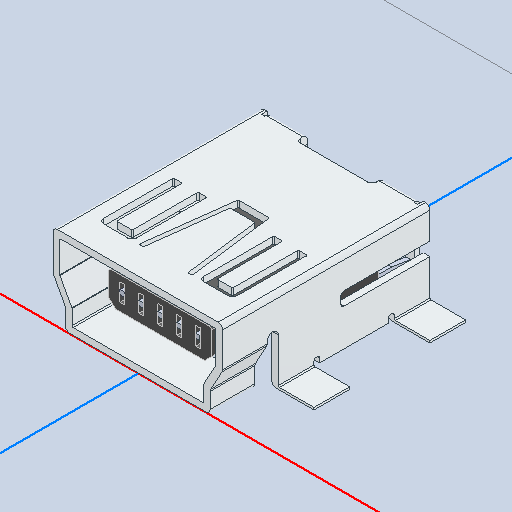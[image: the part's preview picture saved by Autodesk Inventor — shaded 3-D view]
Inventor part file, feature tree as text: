
AUTODESK INVENTOR PART (.ipt)
format: ipt  version: 2022 (Build 260153000, 153)  size: 313,856 bytes
history: native  units: mm
features: other x12, fillet x1, chamfer x1
ambient origin geometry x8: Origin, YZ Plane, XZ Plane, XY Plane, X Axis, Y Axis, Z Axis, Center Point
bodies: Body1 (feature_tree), Body2 (feature_tree), Body3 (feature_tree), Body4 (feature_tree), Body5 (feature_tree), Body6 (feature_tree), Body7 (feature_tree)
feature tree (14):
  other  "Твердое тело1"
  other  "Твердое тело2"
  other  "Твердое тело3"
  other  "Твердое тело4"
  other  "Твердое тело5"
  other  "Твердое тело6"
  other  "Твердое тело7"
  fillet  "Fillet2"  [1 undecoded]
  other  "Boss-Extrude5"
  chamfer  "Chamfer1"  [1 undecoded]
  other  "LPattern1[1]"
  other  "LPattern1[2]"
  other  "LPattern1[3]"
  other  "LPattern1[4]"
note: 2 required parameter values undecoded (feature->parameter linkage not recoverable at this tier; creation-order binding heuristic only, values carry confidence <= 0.55)
